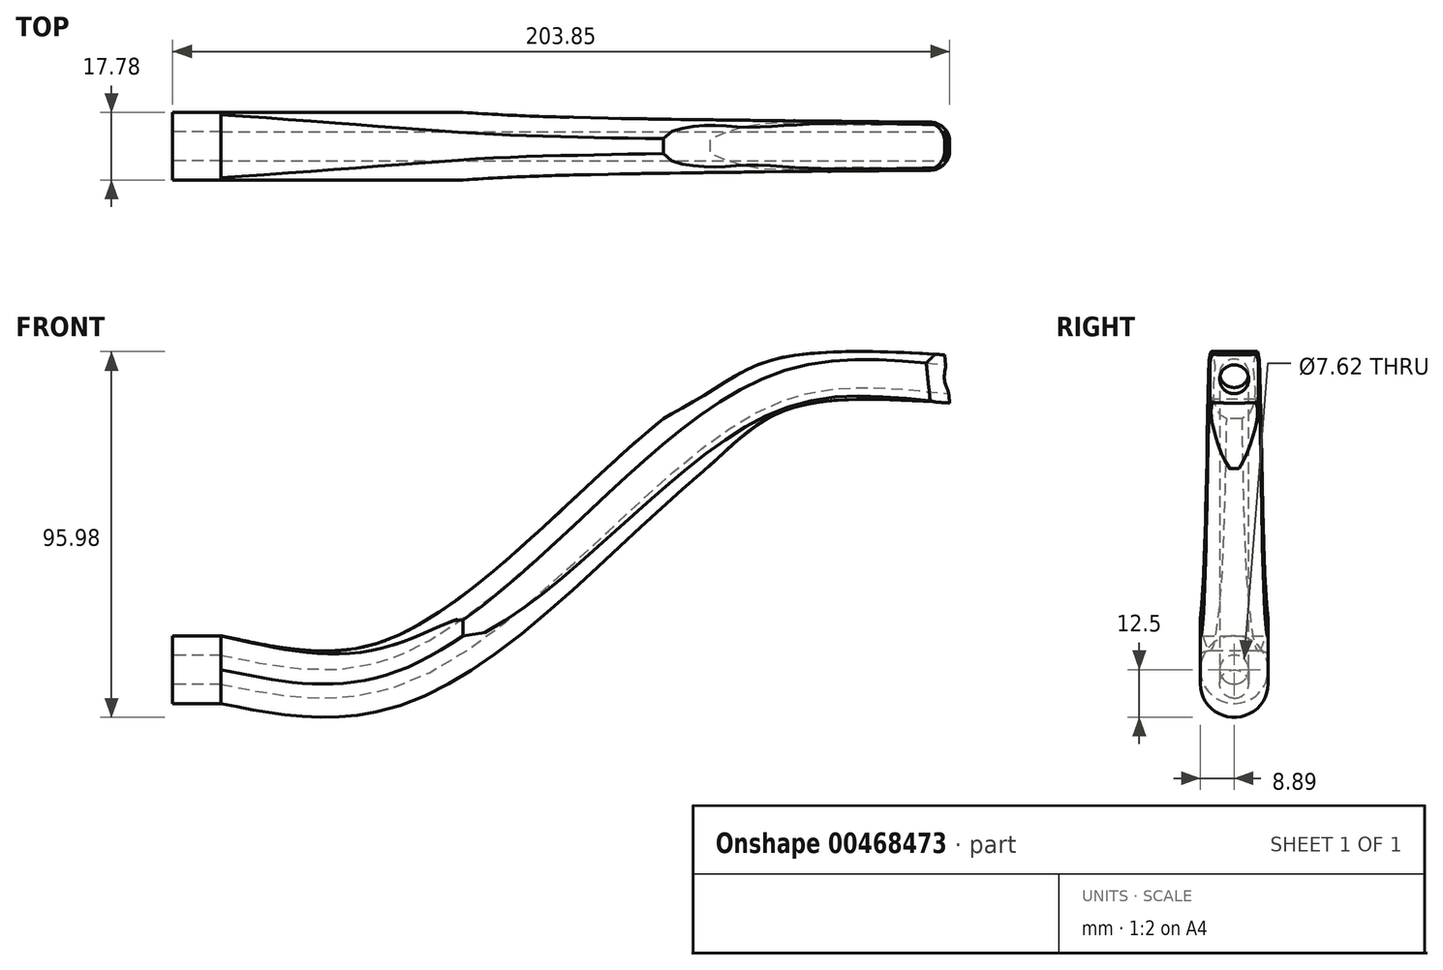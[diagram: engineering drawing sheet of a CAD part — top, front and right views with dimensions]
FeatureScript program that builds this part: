
annotation { "Feature Type Name" : "Feature", "Feature Type Description" : "" }
export const myFeature = defineFeature(function(context is Context, id is Id, definition is map)
    precondition{}
    {
        {
            var Q0;
            Q0=qCreatedBy(makeId("Right.planeOp"),FACE);
            var sketch = newSketch(context, id + "F0", { "sketchPlane" : qUnion([Q0])});
            skCircle(sketch, "E0", {"center": v(0, 0) * mm, "radius": 8.9 * mm});
            skCircle(sketch, "E1", {"center": v(0, 0) * mm, "radius": 3.81 * mm});
            skSolve(sketch);
        }
        {
            var Q0;
            Q0=makeQuery(id+"F0.imprint","IMPRINT",FACE,{"disambiguationData":[TD([[makeQuery(id+"F0.imprint","IMPRINT",EDGE,{"derivedFrom":sQuery(id+"F0.wireOp",EDGE,"E0")}),1.0]])]});
            extrude(context, id + "F1", {"entities" : qUnion([Q0]), "depth" : 12.7 * mm});
        }
        {
            var Q0;
            Q0=makeQuery(id+"F1.opExtrude","CAP_FACE",FACE,{"disambiguationData":[OSD([sQuery(id+"F0.wireOp",EDGE,"E0"),sQuery(id+"F0.wireOp",EDGE,"E1")])],"isStart":false});
            var sketch = newSketch(context, id + "F2", { "sketchPlane" : qUnion([Q0])});
            skLineSegment(sketch, "E2", {"start": v(-8.9, 0) * mm, "end": v(-8.9, 8.9) * mm});
            skLineSegment(sketch, "E3", {"start": v(0, 8.9) * mm, "end": v(-8.9, 8.9) * mm});
            skLineSegment(sketch, "E4", {"start": v(0, 8.9) * mm, "end": v(8.9, 8.9) * mm});
            skLineSegment(sketch, "E5", {"start": v(8.9, 0) * mm, "end": v(8.9, 8.89) * mm});
            skArc(sketch, "E6", {"start": v(-8.9, 0) * mm, "mid": v(0, -8.9) * mm, "end": v(8.9, 0) * mm});
            skCircle(sketch, "E7", {"center": v(0, 0) * mm, "radius": 3.81 * mm});
            skSolve(sketch);
        }
        {
            var Q0;
            Q0=qCreatedBy(makeId("Front.planeOp"),FACE);
            var sketch = newSketch(context, id + "F3", { "sketchPlane" : qUnion([Q0])});
            skLineSegment(sketch, "E8", {"start": v(0, 0) * mm, "end": v(203.2, 0) * mm});
            skLineSegment(sketch, "E9", {"start": v(203.2, 0) * mm, "end": v(203.2, 76.2) * mm});
            skLineSegment(sketch, "E10", {"start": v(0, 0) * mm, "end": v(12.7, 0) * mm});
            skFitSpline(sketch, "E11", {"points": [v(12.7, 0) * mm, v(60.13, 0) * mm, v(126.19, 52.3) * mm, v(165.9, 76.2) * mm, v(203.2, 76.2) * mm], "startDerivative": vector(194.51, -41.37) * mm, "endDerivative": vector(181.47, -19.17) * mm});
            skSolve(sketch);
        }
        {
            var Q0;
            {var subQ0=sQuery(id+"F2.wireOp",EDGE,"E6");Q0=makeQuery(id+"F2.imprint","IMPRINT",FACE,{"disambiguationData":[TD([[makeQuery(id+"F2.imprint","IMPRINT",EDGE,{"derivedFrom":subQ0}),1.0]])]});}
            var Q1;
            {var subQ0=sQuery(id+"F2.wireOp",EDGE,"E4");Q1=makeQuery(id+"F2.imprint","IMPRINT",FACE,{"disambiguationData":[TD([[makeQuery(id+"F2.imprint","IMPRINT",EDGE,{"derivedFrom":subQ0}),-1.0]])]});}
            var Q2;
            {var subQ0=sQuery(id+"F2.wireOp",EDGE,"E2");Q2=makeQuery(id+"F2.imprint","IMPRINT",FACE,{"disambiguationData":[TD([[makeQuery(id+"F2.imprint","IMPRINT",EDGE,{"derivedFrom":subQ0}),-1.0]])]});}
            var Q3;
            Q3=sQuery(id+"F3.wireOp",EDGE,"E11");
            sweep(context, id + "F4", {"operationType" : NewBodyOperationType.ADD, "profiles" : qUnion([Q0, Q1, Q2]), "path" : qUnion([Q3])});
        }
        {
            var Q0;
            Q0=qCreatedBy(makeId("Top.planeOp"),FACE);
            var sketch = newSketch(context, id + "F5", { "sketchPlane" : qUnion([Q0])});
            skLineSegment(sketch, "E12", {"start": v(0, 0) * mm, "end": v(0, 8.9) * mm});
            skLineSegment(sketch, "E13", {"start": v(0, 8.9) * mm, "end": v(76.2, 8.9) * mm});
            skFitSpline(sketch, "E14", {"points": [v(76.2, 8.9) * mm, v(97.67, 7.77) * mm, v(217.59, 6.14) * mm], "startDerivative": vector(57.52, -3.97) * mm, "endDerivative": vector(205.3, -1.82) * mm});
            skLineSegment(sketch, "E15", {"start": v(76.53, 0) * mm, "end": v(134.55, 0) * mm});
            skFitSpline(sketch, "E16.MirrorCS", {"points": [v(76.2, -8.89) * mm, v(97.67, -7.77) * mm, v(217.59, -6.14) * mm], "startDerivative": vector(57.52, 3.97) * mm, "endDerivative": vector(205.3, 1.82) * mm});
            skLineSegment(sketch, "E17", {"start": v(81.9, 22.64) * mm, "end": v(217.22, 13.75) * mm});
            skLineSegment(sketch, "E18", {"start": v(217.22, 13.75) * mm, "end": v(217.59, 6.14) * mm});
            skLineSegment(sketch, "E19", {"start": v(81.9, 22.64) * mm, "end": v(76.2, 8.9) * mm});
            skLineSegment(sketch, "E20", {"start": v(76.2, -8.89) * mm, "end": v(117.07, -29.61) * mm});
            skLineSegment(sketch, "E21", {"start": v(117.07, -29.61) * mm, "end": v(217.59, -6.14) * mm});
            skSolve(sketch);
        }
        {
            var Q0;
            Q0=makeQuery(id+"F5.imprint","IMPRINT",FACE,{"disambiguationData":[TD([[makeQuery(id+"F5.imprint","IMPRINT",EDGE,{"derivedFrom":sQuery(id+"F5.wireOp",EDGE,"E14")}),1.0]])]});
            var Q1;
            Q1=makeQuery(id+"F5.imprint","IMPRINT",FACE,{"disambiguationData":[TD([[makeQuery(id+"F5.imprint","IMPRINT",EDGE,{"derivedFrom":sQuery(id+"F5.wireOp",EDGE,"E16.MirrorCS")}),-1.0]])]});
            extrude(context, id + "F6", {"entities" : qUnion([Q0, Q1]), "operationType" : NewBodyOperationType.REMOVE, "depth" : 101.6 * mm});
        }
        {
            var Q0;
            Q0=qCreatedBy(makeId("Front.planeOp"),FACE);
            var sketch = newSketch(context, id + "F7", { "sketchPlane" : qUnion([Q0])});
            skLineSegment(sketch, "E22", {"start": v(0, 0) * mm, "end": v(76.2, 0) * mm});
            skLineSegment(sketch, "E23", {"start": v(76.2, 0) * mm, "end": v(76.2, -6.2) * mm});
            skLineSegment(sketch, "E24", {"start": v(76.2, 0) * mm, "end": v(76.2, 25.18) * mm});
            skFitSpline(sketch, "E25", {"points": [v(76.2, 25.18) * mm, v(115.72, 57.85) * mm, v(140.62, 72.73) * mm, v(159.38, 81.79) * mm, v(235.4, 79.85) * mm], "startDerivative": vector(146.69, 131.1) * mm, "endDerivative": vector(266.62, -24.43) * mm});
            skLineSegment(sketch, "E26", {"start": v(76.2, 25.18) * mm, "end": v(114.9, 83.75) * mm});
            skLineSegment(sketch, "E27", {"start": v(114.9, 83.75) * mm, "end": v(182.13, 131.48) * mm});
            skLineSegment(sketch, "E28", {"start": v(182.13, 131.48) * mm, "end": v(235.4, 79.85) * mm});
            skFitSpline(sketch, "E29", {"points": [v(76.2, -6.2) * mm, v(133.68, 46.76) * mm, v(158.86, 67.27) * mm, v(192.47, 70.67) * mm, v(247.23, 64.32) * mm, v(167.36, 47.19) * mm, v(113.95, -11.16) * mm, v(97.42, -6.2) * mm, v(96.01, 3.69) * mm, v(90.13, 3.53) * mm, v(76.2, -6.2) * mm]});
            skSolve(sketch);
        }
        {
            var Q0;
            {var subQ0=sQuery(id+"F7.wireOp",EDGE,"E29");var subQ1=sQuery(id+"F7.wireOp",EDGE,"E23");var subQ2=makeQuery(id+"F7.imprint","INTERSECT",VERTEX,{"disambiguationData":[OD(0.0)],"derivedFrom":[subQ1,subQ0]});Q0=makeQuery(id+"F7.imprint","IMPRINT",FACE,{"disambiguationData":[TD([[makeQuery(id+"F7.imprint","IMPRINT",EDGE,{"disambiguationData":[TD([[subQ2,1.0]])],"derivedFrom":subQ1}),1.0]])]});}
            var Q1;
            Q1=makeQuery(id+"F7.imprint","IMPRINT",FACE,{"disambiguationData":[TD([[makeQuery(id+"F7.imprint","IMPRINT",EDGE,{"derivedFrom":sQuery(id+"F7.wireOp",EDGE,"E25")}),1.0]])]});
            extrude(context, id + "F8", {"entities" : qUnion([Q0, Q1]), "operationType" : NewBodyOperationType.REMOVE, "endBound" : BoundingType.SYMMETRIC, "oppositeDirection" : true, "depth" : 50.8 * mm});
        }
        {
            var Q0;
            Q0=makeQuery(id+"F6.boolean.opBoolean","INTERSECT",EDGE,{"derivedFrom":[makeQuery(id+"F4.opSweep","SWEPT_FACE",FACE,{"disambiguationData":[OSD([sQuery(id+"F2.wireOp",EDGE,"E3"),sQuery(id+"F2.wireOp",EDGE,"E4"),sQuery(id+"F3.wireOp",EDGE,"E11")])]}),makeQuery(id+"F6.opExtrude","SWEPT_FACE",FACE,{"disambiguationData":[OSD([sQuery(id+"F5.wireOp",EDGE,"E16.MirrorCS")])]})]});
            var Q1;
            Q1=makeQuery(id+"F6.boolean.opBoolean","INTERSECT",EDGE,{"derivedFrom":[makeQuery(id+"F4.opSweep","SWEPT_FACE",FACE,{"disambiguationData":[OSD([sQuery(id+"F2.wireOp",EDGE,"E3"),sQuery(id+"F2.wireOp",EDGE,"E4"),sQuery(id+"F3.wireOp",EDGE,"E11")])]}),makeQuery(id+"F6.opExtrude","SWEPT_FACE",FACE,{"disambiguationData":[OSD([sQuery(id+"F5.wireOp",EDGE,"E14")])]})]});
            fillet(context, id + "F9", {"entities" : qUnion([Q0, Q1]), "radius" : 5.08 * mm, "tangentPropagation" : true, "allowEdgeOverflow" : false});
        }
        {
            var Q0;
            Q0=makeQuery(id+"F6.boolean.opBoolean","INTERSECT",EDGE,{"derivedFrom":[makeQuery(id+"F4.opSweep","CAP_FACE",FACE,{"disambiguationData":[OSD([sQuery(id+"F2.wireOp",EDGE,"E2"),sQuery(id+"F2.wireOp",EDGE,"E3"),sQuery(id+"F2.wireOp",EDGE,"E4"),sQuery(id+"F2.wireOp",EDGE,"E5"),sQuery(id+"F2.wireOp",EDGE,"E6"),sQuery(id+"F2.wireOp",EDGE,"E7"),sQuery(id+"F3.wireOp",VERTEX,"E11.end")])],"isStart":false}),makeQuery(id+"F6.opExtrude","SWEPT_FACE",FACE,{"disambiguationData":[OSD([sQuery(id+"F5.wireOp",EDGE,"E16.MirrorCS")])]})]});
            var Q1;
            Q1=makeQuery(id+"F6.boolean.opBoolean","INTERSECT",EDGE,{"derivedFrom":[makeQuery(id+"F4.opSweep","CAP_FACE",FACE,{"disambiguationData":[OSD([sQuery(id+"F2.wireOp",EDGE,"E2"),sQuery(id+"F2.wireOp",EDGE,"E3"),sQuery(id+"F2.wireOp",EDGE,"E4"),sQuery(id+"F2.wireOp",EDGE,"E5"),sQuery(id+"F2.wireOp",EDGE,"E6"),sQuery(id+"F2.wireOp",EDGE,"E7"),sQuery(id+"F3.wireOp",VERTEX,"E11.end")])],"isStart":false}),makeQuery(id+"F6.opExtrude","SWEPT_FACE",FACE,{"disambiguationData":[OSD([sQuery(id+"F5.wireOp",EDGE,"E14")])]})]});
            fillet(context, id + "F10", {"entities" : qUnion([Q0, Q1]), "radius" : 5.08 * mm, "tangentPropagation" : true, "allowEdgeOverflow" : false});
        }
    });
